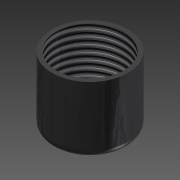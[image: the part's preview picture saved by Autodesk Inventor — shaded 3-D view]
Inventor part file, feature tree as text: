
AUTODESK INVENTOR PART (.ipt)
format: ipt  version: 2015 (Build 190159000, 159)  size: 124,928 bytes
history: native  units: mm
features: other x1, extrude x1, shell x1, thread x1, fillet x1, sketch x1
ambient origin geometry x8: Origin, YZ Plane, XZ Plane, XY Plane, X Axis, Y Axis, Z Axis, Center Point
bodies: Body1 (feature_tree)
feature tree (6):
  other  "Bryła1"
  extrude  "Wyciągnięcie proste1"  Depth=9.0mm
  shell  "Skorupa1"  Thickness=8.0mm
  thread  "Gwint1"
  fillet  "Zaokrąglenie1"  Radius=0.5mm
  sketch  "Szkic1"
